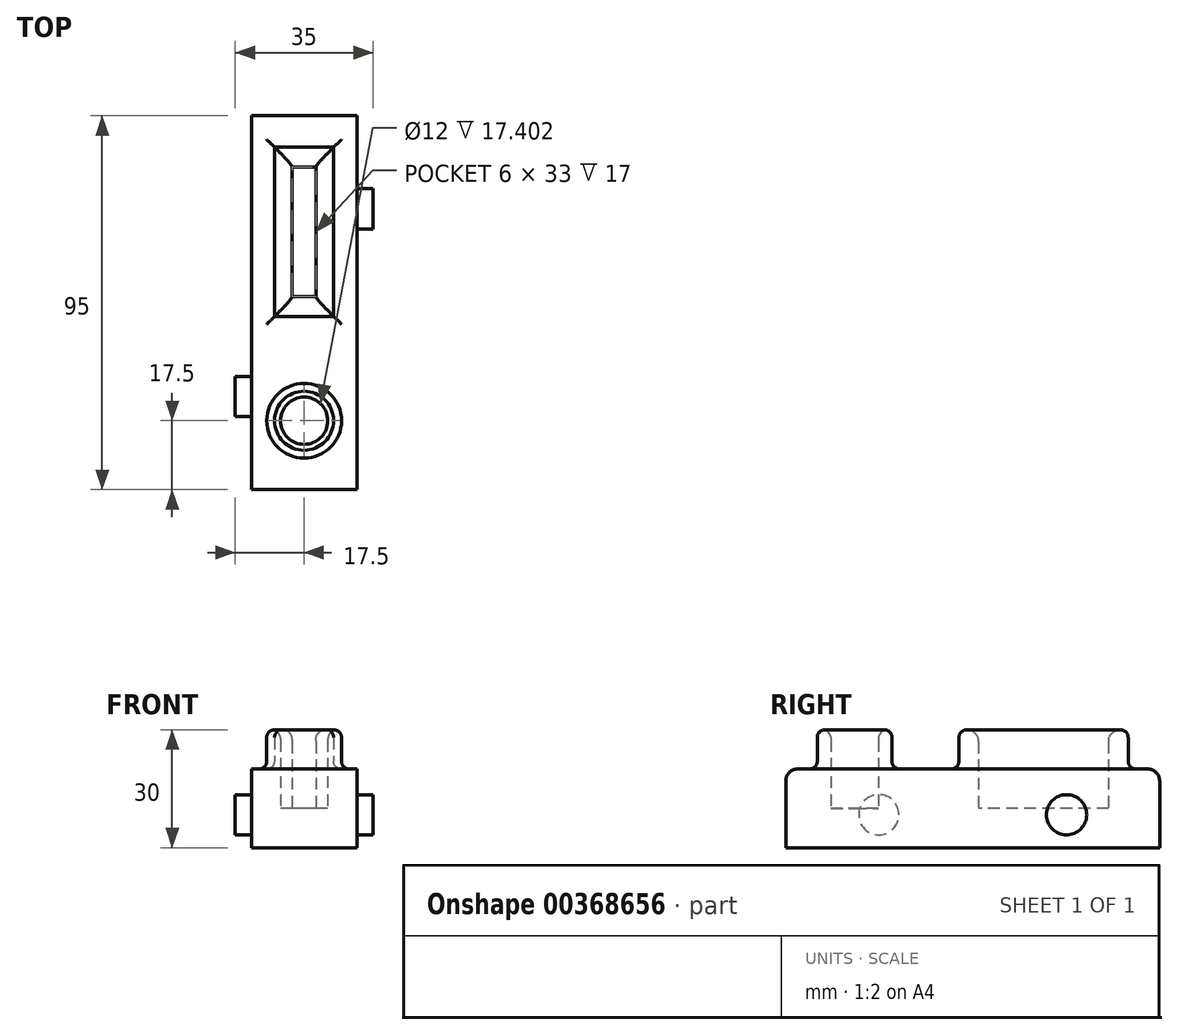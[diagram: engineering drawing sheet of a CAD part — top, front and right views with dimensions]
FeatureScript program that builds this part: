
annotation { "Feature Type Name" : "Feature", "Feature Type Description" : "" }
export const myFeature = defineFeature(function(context is Context, id is Id, definition is map)
    precondition{}
    {
        {
            var Q0;
            Q0=qCreatedBy(makeId("Top.planeOp"),FACE);
            var sketch = newSketch(context, id + "F0", { "sketchPlane" : qUnion([Q0])});
            skLineSegment(sketch, "E0.bottom", {"start": v(-17.5, 47.5) * mm, "end": v(17.5, 47.5) * mm});
            skLineSegment(sketch, "E0.top", {"start": v(-17.5, -47.5) * mm, "end": v(17.5, -47.5) * mm});
            skLineSegment(sketch, "E0.left", {"start": v(-17.5, 47.5) * mm, "end": v(-17.5, -47.5) * mm});
            skLineSegment(sketch, "E0.right", {"start": v(17.5, 47.5) * mm, "end": v(17.5, -47.5) * mm});
            skPoint(sketch, "E0.middle", {"position": v(0, 0) * mm});
            skSolve(sketch);
        }
        {
            var Q0;
            Q0=makeQuery(id+"F0.imprint","IMPRINT",FACE,{"disambiguationData":[TD([[makeQuery(id+"F0.imprint","IMPRINT",EDGE,{"derivedFrom":sQuery(id+"F0.wireOp",EDGE,"E0.bottom")}),-1.0]])]});
            extrude(context, id + "F1", {"entities" : qUnion([Q0]), "endBound" : BoundingType.SYMMETRIC, "depth" : 20 * mm});
        }
        {
            var Q0;
            Q0=makeQuery(id+"F1.opExtrude","CAP_FACE",FACE,{"disambiguationData":[OSD([sQuery(id+"F0.wireOp",EDGE,"E0.bottom"),sQuery(id+"F0.wireOp",EDGE,"E0.top"),sQuery(id+"F0.wireOp",EDGE,"E0.left"),sQuery(id+"F0.wireOp",EDGE,"E0.right")])],"isStart":false});
            var sketch = newSketch(context, id + "F2", { "sketchPlane" : qUnion([Q0])});
            skLineSegment(sketch, "E1.bottom", {"start": v(7.5, 39.5) * mm, "end": v(-7.5, 39.5) * mm});
            skLineSegment(sketch, "E1.top", {"start": v(7.5, -3.5) * mm, "end": v(-7.5, -3.5) * mm});
            skLineSegment(sketch, "E1.left", {"start": v(7.5, 39.5) * mm, "end": v(7.5, -3.5) * mm});
            skLineSegment(sketch, "E1.right", {"start": v(-7.5, 39.5) * mm, "end": v(-7.5, -3.5) * mm});
            skPoint(sketch, "E1.middle", {"position": v(0, 18) * mm});
            skLineSegment(sketch, "E2.bottom", {"start": v(3, 34.5) * mm, "end": v(-3, 34.5) * mm});
            skLineSegment(sketch, "E2.top", {"start": v(3, 1.5) * mm, "end": v(-3, 1.5) * mm});
            skLineSegment(sketch, "E2.left", {"start": v(3, 34.5) * mm, "end": v(3, 1.5) * mm});
            skLineSegment(sketch, "E2.right", {"start": v(-3, 34.5) * mm, "end": v(-3, 1.5) * mm});
            skCircle(sketch, "E3", {"center": v(0, -30) * mm, "radius": 6 * mm});
            skCircle(sketch, "E4.0", {"center": v(0, -30) * mm, "radius": 9.5 * mm});
            skLineSegment(sketch, "E5", {"start": v(0, -47.5) * mm, "end": v(0, -30) * mm, "construction": true});
            skSolve(sketch);
        }
        {
            var Q0;
            Q0=makeQuery(id+"F2.imprint","IMPRINT",FACE,{"disambiguationData":[TD([[makeQuery(id+"F2.imprint","IMPRINT",EDGE,{"derivedFrom":sQuery(id+"F2.wireOp",EDGE,"E1.bottom")}),1.0]])]});
            var Q1;
            Q1=makeQuery(id+"F2.imprint","IMPRINT",FACE,{"disambiguationData":[TD([[makeQuery(id+"F2.imprint","IMPRINT",EDGE,{"derivedFrom":sQuery(id+"F2.wireOp",EDGE,"E3")}),-1.0]])]});
            extrude(context, id + "F3", {"entities" : qUnion([Q0, Q1]), "operationType" : NewBodyOperationType.ADD, "depth" : 10 * mm});
        }
        {
            var Q0;
            Q0=makeQuery(id+"F3.boolean.opBoolean","SPLIT",FACE,{"disambiguationData":[TD([makeQuery(id+"F3.opExtrude","SWEPT_FACE",FACE,{"disambiguationData":[OSD([sQuery(id+"F2.wireOp",EDGE,"E2.bottom")])]})])],"derivedFrom":makeQuery(id+"F1.opExtrude","CAP_FACE",FACE,{"disambiguationData":[OSD([sQuery(id+"F0.wireOp",EDGE,"E0.bottom"),sQuery(id+"F0.wireOp",EDGE,"E0.top"),sQuery(id+"F0.wireOp",EDGE,"E0.left"),sQuery(id+"F0.wireOp",EDGE,"E0.right")])],"isStart":false})});
            var Q1;
            Q1=makeQuery(id+"F3.boolean.opBoolean","SPLIT",FACE,{"disambiguationData":[TD([makeQuery(id+"F3.opExtrude","SWEPT_FACE",FACE,{"disambiguationData":[OSD([sQuery(id+"F2.wireOp",EDGE,"E3")])]})])],"derivedFrom":makeQuery(id+"F1.opExtrude","CAP_FACE",FACE,{"disambiguationData":[OSD([sQuery(id+"F0.wireOp",EDGE,"E0.bottom"),sQuery(id+"F0.wireOp",EDGE,"E0.top"),sQuery(id+"F0.wireOp",EDGE,"E0.left"),sQuery(id+"F0.wireOp",EDGE,"E0.right")])],"isStart":false})});
            extrude(context, id + "F4", {"entities" : qUnion([Q0, Q1]), "operationType" : NewBodyOperationType.REMOVE, "oppositeDirection" : true, "depth" : 10 * mm});
        }
        {
            var Q0;
            Q0=makeQuery(id+"F1.opExtrude","CAP_EDGE",EDGE,{"disambiguationData":[OSD([sQuery(id+"F0.wireOp",EDGE,"E0.top")])],"isStart":false});
            var Q1;
            Q1=makeQuery(id+"F1.opExtrude","CAP_EDGE",EDGE,{"disambiguationData":[OSD([sQuery(id+"F0.wireOp",EDGE,"E0.bottom")])],"isStart":false});
            fillet(context, id + "F5", {"entities" : qUnion([Q0, Q1]), "radius" : 3 * mm, "tangentPropagation" : true, "allowEdgeOverflow" : false});
        }
        {
            var Q0;
            Q0=makeQuery(id+"F3.opExtrude","CAP_EDGE",EDGE,{"disambiguationData":[OSD([sQuery(id+"F2.wireOp",EDGE,"E1.left")])],"isStart":false});
            var Q1;
            Q1=makeQuery(id+"F3.opExtrude","CAP_EDGE",EDGE,{"disambiguationData":[OSD([sQuery(id+"F2.wireOp",EDGE,"E1.top")])],"isStart":false});
            var Q2;
            Q2=makeQuery(id+"F3.opExtrude","CAP_EDGE",EDGE,{"disambiguationData":[OSD([sQuery(id+"F2.wireOp",EDGE,"E1.right")])],"isStart":false});
            var Q3;
            Q3=makeQuery(id+"F3.opExtrude","CAP_EDGE",EDGE,{"disambiguationData":[OSD([sQuery(id+"F2.wireOp",EDGE,"E1.bottom")])],"isStart":false});
            var Q4;
            Q4=makeQuery(id+"F3.opExtrude","CAP_EDGE",EDGE,{"disambiguationData":[OSD([sQuery(id+"F2.wireOp",EDGE,"E4.0")])],"isStart":false});
            fillet(context, id + "F6", {"entities" : qUnion([Q0, Q1, Q2, Q3, Q4]), "radius" : 2 * mm, "allowEdgeOverflow" : false});
        }
        {
            var Q0;
            Q0=makeQuery(id+"F3.opExtrude","CAP_EDGE",EDGE,{"disambiguationData":[OSD([sQuery(id+"F2.wireOp",EDGE,"E2.right")])],"isStart":false});
            var Q1;
            Q1=makeQuery(id+"F3.opExtrude","CAP_EDGE",EDGE,{"disambiguationData":[OSD([sQuery(id+"F2.wireOp",EDGE,"E2.left")])],"isStart":false});
            fillet(context, id + "F7", {"entities" : qUnion([Q0, Q1]), "radius" : 2.5 * mm, "tangentPropagation" : true, "allowEdgeOverflow" : false});
        }
        {
            var Q0;
            Q0=makeQuery(id+"F3.opExtrude","CAP_EDGE",EDGE,{"disambiguationData":[OSD([sQuery(id+"F2.wireOp",EDGE,"E2.bottom")])],"isStart":false});
            var Q1;
            Q1=makeQuery(id+"F3.opExtrude","CAP_EDGE",EDGE,{"disambiguationData":[OSD([sQuery(id+"F2.wireOp",EDGE,"E2.top")])],"isStart":false});
            var Q2;
            Q2=makeQuery(id+"F3.opExtrude","CAP_EDGE",EDGE,{"disambiguationData":[OSD([sQuery(id+"F2.wireOp",EDGE,"E3")])],"isStart":false});
            fillet(context, id + "F8", {"entities" : qUnion([Q0, Q1, Q2]), "radius" : 3 * mm, "tangentPropagation" : true, "allowEdgeOverflow" : false});
        }
        {
            var Q0;
            Q0=makeQuery(id+"F3.opExtrude","CAP_EDGE",EDGE,{"disambiguationData":[OSD([sQuery(id+"F2.wireOp",EDGE,"E1.bottom")])],"isStart":true});
            var Q1;
            Q1=makeQuery(id+"F3.opExtrude","CAP_EDGE",EDGE,{"disambiguationData":[OSD([sQuery(id+"F2.wireOp",EDGE,"E1.right")])],"isStart":true});
            var Q2;
            Q2=makeQuery(id+"F3.opExtrude","CAP_EDGE",EDGE,{"disambiguationData":[OSD([sQuery(id+"F2.wireOp",EDGE,"E1.top")])],"isStart":true});
            var Q3;
            Q3=makeQuery(id+"F3.opExtrude","CAP_EDGE",EDGE,{"disambiguationData":[OSD([sQuery(id+"F2.wireOp",EDGE,"E1.left")])],"isStart":true});
            var Q4;
            Q4=makeQuery(id+"F3.opExtrude","CAP_EDGE",EDGE,{"disambiguationData":[OSD([sQuery(id+"F2.wireOp",EDGE,"E4.0")])],"isStart":true});
            fillet(context, id + "F9", {"entities" : qUnion([Q0, Q1, Q2, Q3, Q4]), "radius" : 2 * mm, "tangentPropagation" : true, "allowEdgeOverflow" : false});
        }
        {
            var Q0;
            Q0=makeQuery(id+"F1.opExtrude","SWEPT_FACE",FACE,{"disambiguationData":[OSD([sQuery(id+"F0.wireOp",EDGE,"E0.right")])]});
            var sketch = newSketch(context, id + "F10", { "sketchPlane" : qUnion([Q0])});
            skCircle(sketch, "E6", {"center": v(-23.85, -1.6) * mm, "radius": 5.1 * mm});
            skCircle(sketch, "E7.MirrorC", {"center": v(23.85, -1.6) * mm, "radius": 5.1 * mm});
            skSolve(sketch);
        }
        {
            var Q0;
            Q0=makeQuery(id+"F10.imprint","IMPRINT",FACE,{"disambiguationData":[TD([[makeQuery(id+"F10.imprint","IMPRINT",EDGE,{"derivedFrom":sQuery(id+"F10.wireOp",EDGE,"E6")}),1.0]])]});
            var Q1;
            Q1=makeQuery(id+"F10.imprint","IMPRINT",FACE,{"disambiguationData":[TD([[makeQuery(id+"F10.imprint","IMPRINT",EDGE,{"derivedFrom":sQuery(id+"F10.wireOp",EDGE,"E7.MirrorC")}),-1.0]])]});
            extrude(context, id + "F11", {"entities" : qUnion([Q0, Q1]), "operationType" : NewBodyOperationType.REMOVE, "oppositeDirection" : true, "depth" : 4.1 * mm});
        }
        {
            var Q0;
            Q0=makeQuery(id+"F1.opExtrude","SWEPT_FACE",FACE,{"disambiguationData":[OSD([sQuery(id+"F0.wireOp",EDGE,"E0.left")])]});
            var sketch = newSketch(context, id + "F12", { "sketchPlane" : qUnion([Q0])});
            skCircle(sketch, "E8", {"center": v(-23.85, -1.6) * mm, "radius": 5.1 * mm});
            skCircle(sketch, "E9.MirrorC", {"center": v(23.85, -1.6) * mm, "radius": 5.1 * mm});
            skSolve(sketch);
        }
        {
            var Q0;
            Q0=makeQuery(id+"F12.imprint","IMPRINT",FACE,{"disambiguationData":[TD([[makeQuery(id+"F12.imprint","IMPRINT",EDGE,{"derivedFrom":sQuery(id+"F12.wireOp",EDGE,"E8")}),1.0]])]});
            var Q1;
            Q1=makeQuery(id+"F12.imprint","IMPRINT",FACE,{"disambiguationData":[TD([[makeQuery(id+"F12.imprint","IMPRINT",EDGE,{"derivedFrom":sQuery(id+"F12.wireOp",EDGE,"E9.MirrorC")}),-1.0]])]});
            extrude(context, id + "F13", {"entities" : qUnion([Q0, Q1]), "operationType" : NewBodyOperationType.REMOVE, "oppositeDirection" : true, "depth" : 4.1 * mm});
        }
    });
